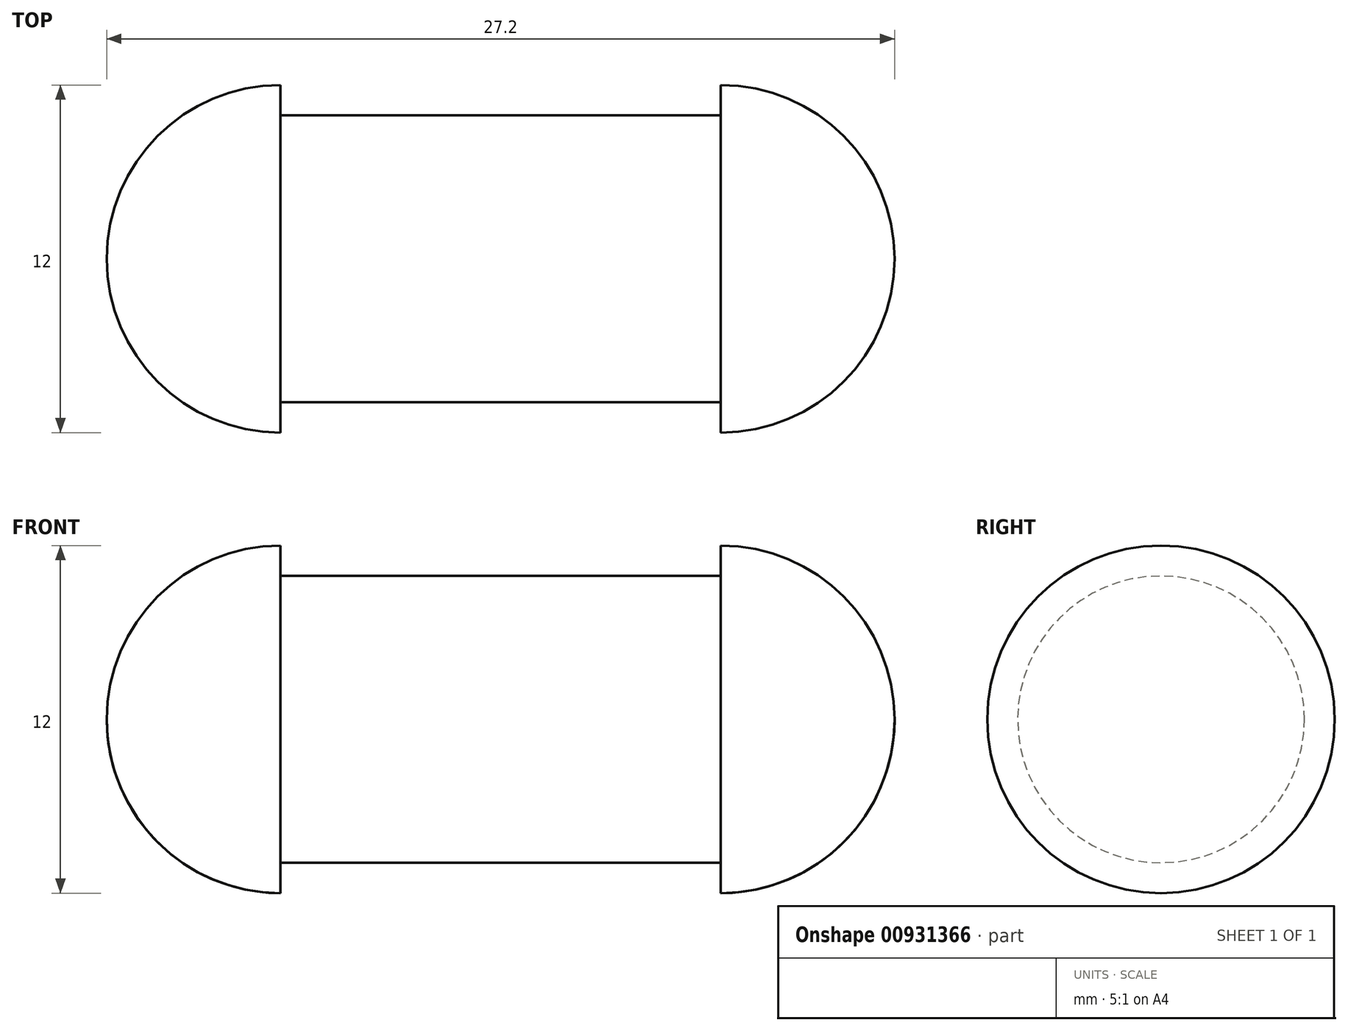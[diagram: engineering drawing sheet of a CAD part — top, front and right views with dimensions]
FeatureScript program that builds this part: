
annotation { "Feature Type Name" : "Feature", "Feature Type Description" : "" }
export const myFeature = defineFeature(function(context is Context, id is Id, definition is map)
    precondition{}
    {
        {
            var Q0;
            Q0=qCreatedBy(makeId("Front.planeOp"),FACE);
            var sketch = newSketch(context, id + "F0", { "sketchPlane" : qUnion([Q0])});
            skLineSegment(sketch, "E0", {"start": v(0, 0) * mm, "end": v(13.6, 0) * mm});
            skLineSegment(sketch, "E1", {"start": v(0, 0) * mm, "end": v(0, 4.95) * mm});
            skLineSegment(sketch, "E2", {"start": v(0, 4.95) * mm, "end": v(7.6, 4.95) * mm});
            skArc(sketch, "E3", {"start": v(13.6, 0) * mm, "mid": v(11.84, 4.24) * mm, "end": v(7.6, 6) * mm});
            skLineSegment(sketch, "E4", {"start": v(7.6, 6) * mm, "end": v(7.6, 4.95) * mm});
            skSolve(sketch);
        }
        {
            var Q0;
            Q0 = qSketchRegion(id + "F0", true);
            var Q1;
            Q1=sQuery(id+"F0.wireOp",EDGE,"E0");
            revolve(context, id + "F1", {"surfaceOperationType" : NewSurfaceOperationType.NEW, "entities" : qUnion([Q0]), "axis" : qUnion([Q1]), "revolveType" : RevolveType.FULL});
        }
        {
            var Q0;
            Q0=makeQuery(id+"F1.opRevolve","SWEPT_BODY",BODY,{"disambiguationData":[OSD([sQuery(id+"F0.wireOp",EDGE,"E0"),sQuery(id+"F0.wireOp",EDGE,"E1"),sQuery(id+"F0.wireOp",EDGE,"E2"),sQuery(id+"F0.wireOp",EDGE,"E3"),sQuery(id+"F0.wireOp",EDGE,"E4")])]});
            var Q1;
            Q1=makeQuery(id+"F1.opRevolve","SWEPT_FACE",FACE,{"disambiguationData":[OSD([sQuery(id+"F0.wireOp",EDGE,"E1")])]});
            mirror(context, id + "F2", {"operationType" : NewBodyOperationType.ADD, "entities" : qUnion([Q0]), "mirrorPlane" : qUnion([Q1])});
        }
    });
